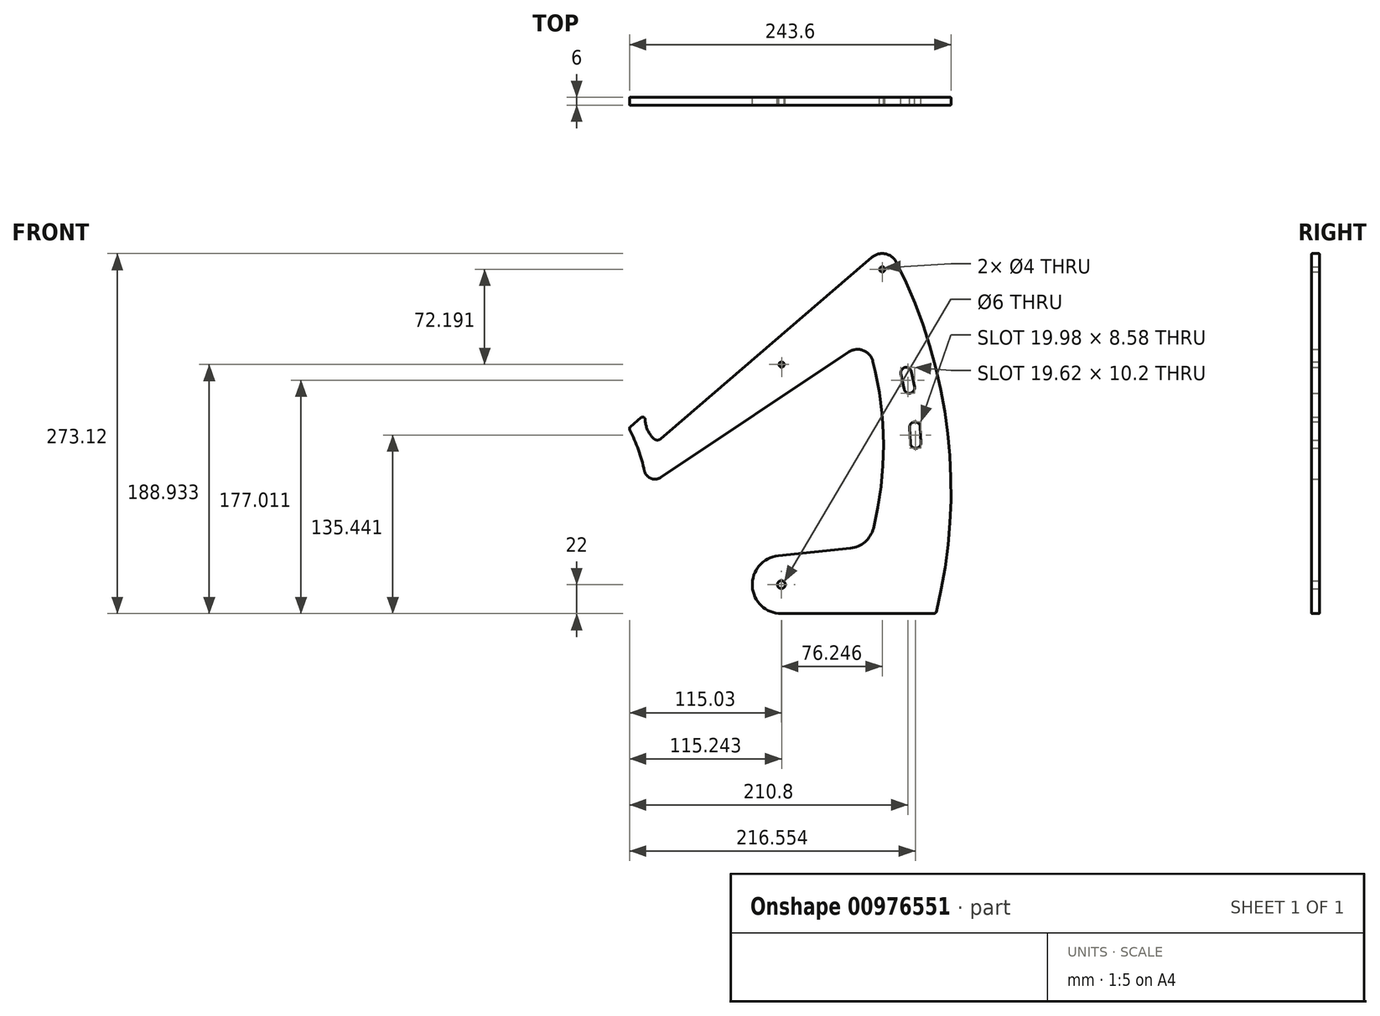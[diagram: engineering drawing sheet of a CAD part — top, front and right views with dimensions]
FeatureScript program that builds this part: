
annotation { "Feature Type Name" : "Feature", "Feature Type Description" : "" }
export const myFeature = defineFeature(function(context is Context, id is Id, definition is map)
    precondition{}
    {
        {
            var Q0;
            Q0=qCreatedBy(makeId("Front.planeOp"),FACE);
            var sketch = newSketch(context, id + "F0", { "sketchPlane" : qUnion([Q0])});
            skLineSegment(sketch, "E0", {"start": v(105, 0) * mm, "end": v(222, 0) * mm});
            skArc(sketch, "E1", {"start": v(3.38, 96.54) * mm, "mid": v(-1.65, 119.28) * mm, "end": v(-10.52, 140.81) * mm});
            skArc(sketch, "E2", {"start": v(222, 0) * mm, "mid": v(230.27, 143.54) * mm, "end": v(185, 280) * mm});
            skLineSegment(sketch, "E3", {"start": v(185, 280) * mm, "end": v(10.64, 130) * mm});
            skLineSegment(sketch, "E4", {"start": v(185, 280) * mm, "end": v(222, 0) * mm, "construction": true});
            skLineSegment(sketch, "E5", {"start": v(10.64, 130) * mm, "end": v(2.37, 151.9) * mm, "construction": true});
            skLineSegment(sketch, "E6", {"start": v(2.37, 151.9) * mm, "end": v(-10.52, 140.81) * mm});
            skArc(sketch, "E7", {"start": v(102.7, 43.88) * mm, "mid": v(83.03, 20.85) * mm, "end": v(105, 0) * mm});
            skLineSegment(sketch, "E8", {"start": v(3.38, 96.54) * mm, "end": v(169.76, 207.53) * mm});
            skLineSegment(sketch, "E9", {"start": v(102.7, 43.88) * mm, "end": v(171, 51.06) * mm});
            skArc(sketch, "E10", {"start": v(171, 51.06) * mm, "mid": v(182.38, 129.39) * mm, "end": v(169.76, 207.53) * mm});
            skLineSegment(sketch, "E11", {"start": v(169.76, 207.53) * mm, "end": v(171, 51.06) * mm, "construction": true});
            skArc(sketch, "E12", {"start": v(2.37, 151.9) * mm, "mid": v(2.5, 142.7) * mm, "end": v(6.73, 134.55) * mm});
            skLineSegment(sketch, "E13", {"start": v(-3.7, 146.68) * mm, "end": v(10.64, 130) * mm, "construction": true});
            skLineSegment(sketch, "E14", {"start": v(6.73, 134.55) * mm, "end": v(10.64, 130) * mm});
            skSolve(sketch);
        }
        {
            var Q0;
            Q0=makeQuery(id+"F0.imprint","IMPRINT",FACE,{"disambiguationData":[TD([[makeQuery(id+"F0.imprint","IMPRINT",EDGE,{"derivedFrom":sQuery(id+"F0.wireOp",EDGE,"E0")}),1.0]])]});
            extrude(context, id + "F1", {"entities" : qUnion([Q0]), "depth" : 6 * mm, "offsetDistance" : 25 * mm});
        }
        {
            var Q0;
            Q0=qCreatedBy(makeId("Front.planeOp"),FACE);
            var sketch = newSketch(context, id + "F2", { "sketchPlane" : qUnion([Q0])});
            skLineSegment(sketch, "E15", {"start": v(199.6, 182.9) * mm, "end": v(177.33, 178.45) * mm, "construction": true});
            skLineSegment(sketch, "E16", {"start": v(199.6, 182.9) * mm, "end": v(221.86, 187.34) * mm, "construction": true});
            skLineSegment(sketch, "E17", {"start": v(195.67, 182.11) * mm, "end": v(198.02, 170.34) * mm});
            skLineSegment(sketch, "E18", {"start": v(203.52, 183.68) * mm, "end": v(205.87, 171.91) * mm});
            skArc(sketch, "E19", {"start": v(203.52, 183.68) * mm, "mid": v(198.81, 186.82) * mm, "end": v(195.67, 182.11) * mm});
            skArc(sketch, "E20", {"start": v(198.02, 170.34) * mm, "mid": v(202.73, 167.2) * mm, "end": v(205.87, 171.91) * mm});
            skLineSegment(sketch, "E21", {"start": v(206.23, 141.43) * mm, "end": v(182.07, 140.24) * mm, "construction": true});
            skLineSegment(sketch, "E22", {"start": v(206.23, 141.43) * mm, "end": v(230.39, 142.63) * mm, "construction": true});
            skLineSegment(sketch, "E23", {"start": v(202.23, 141.24) * mm, "end": v(202.83, 129.25) * mm});
            skLineSegment(sketch, "E24", {"start": v(210.22, 141.63) * mm, "end": v(210.82, 129.65) * mm});
            skArc(sketch, "E25", {"start": v(210.22, 141.63) * mm, "mid": v(206.03, 145.43) * mm, "end": v(202.23, 141.24) * mm});
            skArc(sketch, "E26", {"start": v(202.83, 129.25) * mm, "mid": v(207.02, 125.45) * mm, "end": v(210.82, 129.65) * mm});
            skSolve(sketch);
        }
        {
            var Q0;
            Q0 = qSketchRegion(id + "F2", true);
            extrude(context, id + "F3", {"entities" : qUnion([Q0]), "operationType" : NewBodyOperationType.REMOVE, "endBound" : BoundingType.THROUGH_ALL, "depth" : 25 * mm, "offsetDistance" : 25 * mm});
        }
        {
            var Q0;
            Q0=makeQuery(id+"F1.opExtrude","SWEPT_EDGE",EDGE,{"disambiguationData":[OSD([sQuery(id+"F0.wireOp",EDGE,"E2"),sQuery(id+"F0.wireOp",EDGE,"E3")])]});
            fillet(context, id + "F4", {"entities" : qUnion([Q0]), "radius" : 12 * mm, "tangentPropagation" : true, "defaultsChanged" : true, "vertexSettings" : [], "allowEdgeOverflow" : false});
        }
        {
            var Q0;
            Q0=makeQuery(id+"F1.opExtrude","SWEPT_EDGE",EDGE,{"disambiguationData":[OSD([sQuery(id+"F0.wireOp",EDGE,"E1"),sQuery(id+"F0.wireOp",EDGE,"E8")])]});
            fillet(context, id + "F5", {"entities" : qUnion([Q0]), "radius" : 8 * mm, "tangentPropagation" : true, "allowEdgeOverflow" : false});
        }
        {
            var Q0;
            Q0=makeQuery(id+"F1.opExtrude","SWEPT_EDGE",EDGE,{"disambiguationData":[OSD([sQuery(id+"F0.wireOp",EDGE,"E3"),sQuery(id+"F0.wireOp",EDGE,"E5")])]});
            fillet(context, id + "F6", {"entities" : qUnion([Q0]), "radius" : 4 * mm, "tangentPropagation" : true, "defaultsChanged" : true, "vertexSettings" : [], "allowEdgeOverflow" : false});
        }
        {
            var Q0;
            Q0=makeQuery(id+"F1.opExtrude","SWEPT_EDGE",EDGE,{"disambiguationData":[OSD([sQuery(id+"F0.wireOp",EDGE,"E9"),sQuery(id+"F0.wireOp",EDGE,"E10")])]});
            fillet(context, id + "F7", {"entities" : qUnion([Q0]), "radius" : 20 * mm, "tangentPropagation" : true, "defaultsChanged" : false, "vertexSettings" : [], "allowEdgeOverflow" : false});
        }
        {
            var Q0;
            Q0=makeQuery(id+"F1.opExtrude","SWEPT_EDGE",EDGE,{"disambiguationData":[OSD([sQuery(id+"F0.wireOp",EDGE,"E8"),sQuery(id+"F0.wireOp",EDGE,"E10")])]});
            fillet(context, id + "F8", {"entities" : qUnion([Q0]), "tangentPropagation" : true, "radius" : 12 * mm, "defaultsChanged" : true, "vertexSettings" : [], "allowEdgeOverflow" : false});
        }
        {
            var Q0;
            Q0=qCreatedBy(makeId("Front.planeOp"),FACE);
            var sketch = newSketch(context, id + "F9", { "sketchPlane" : qUnion([Q0])});
            skPoint(sketch, "E27", {"position": v(105, 22) * mm});
            skSolve(sketch);
        }
        {
            var Q0;
            Q0=sQuery(id+"F9.wireOp",VERTEX,"E27");
            var Q1;
            Q1=makeQuery(id+"F1.opExtrude","SWEPT_BODY",BODY,{"disambiguationData":[OSD([sQuery(id+"F0.wireOp",EDGE,"E0"),sQuery(id+"F0.wireOp",EDGE,"E1"),sQuery(id+"F0.wireOp",EDGE,"E2"),sQuery(id+"F0.wireOp",EDGE,"E3"),sQuery(id+"F0.wireOp",EDGE,"E5"),sQuery(id+"F0.wireOp",EDGE,"E6")])]});
            hole(context, id + "F10", {"style" : HoleStyle.SIMPLE, "endStyle" : HoleEndStyle.THROUGH, "oppositeDirection" : true, "holeDiameter" : 6 * mm, "majorDiameter" : 5 * mm, "isTappedThrough" : true, "tappedDepth" : 12 * mm, "tapClearance" : 3, "locations" : qUnion([Q0]), "scope" : qUnion([Q1])});
        }
        {
            var Q0;
            Q0=qCreatedBy(makeId("Front.planeOp"),FACE);
            var sketch = newSketch(context, id + "F11", { "sketchPlane" : qUnion([Q0])});
            skPoint(sketch, "E28", {"position": v(181.46, 261.12) * mm});
            skPoint(sketch, "E29", {"position": v(105.21, 188.93) * mm});
            skLineSegment(sketch, "E30", {"start": v(181.46, 261.12) * mm, "end": v(105.21, 188.93) * mm, "construction": true});
            skSolve(sketch);
        }
        {
            var Q0;
            Q0=sQuery(id+"F11.wireOp",VERTEX,"E29");
            var Q1;
            Q1=sQuery(id+"F11.wireOp",VERTEX,"E28");
            var Q2;
            Q2=makeQuery(id+"F1.opExtrude","SWEPT_BODY",BODY,{"disambiguationData":[OSD([sQuery(id+"F0.wireOp",EDGE,"E0"),sQuery(id+"F0.wireOp",EDGE,"E1"),sQuery(id+"F0.wireOp",EDGE,"E2"),sQuery(id+"F0.wireOp",EDGE,"E3"),sQuery(id+"F0.wireOp",EDGE,"E5"),sQuery(id+"F0.wireOp",EDGE,"E6"),sQuery(id+"F0.wireOp",EDGE,"E7"),sQuery(id+"F0.wireOp",EDGE,"E8"),sQuery(id+"F0.wireOp",EDGE,"E9"),sQuery(id+"F0.wireOp",EDGE,"E10")])]});
            hole(context, id + "F12", {"style" : HoleStyle.SIMPLE, "endStyle" : HoleEndStyle.THROUGH, "oppositeDirection" : true, "holeDiameter" : 4 * mm, "majorDiameter" : 5 * mm, "isTappedThrough" : true, "tappedDepth" : 12 * mm, "tapClearance" : 3, "locations" : qUnion([Q0, Q1]), "scope" : qUnion([Q2])});
        }
        {
            var Q0;
            Q0=makeQuery(id+"F1.opExtrude","SWEPT_EDGE",EDGE,{"disambiguationData":[OSD([sQuery(id+"F0.wireOp",EDGE,"E1"),sQuery(id+"F0.wireOp",EDGE,"E6")])]});
            var Q1;
            Q1=makeQuery(id+"F1.opExtrude","SWEPT_EDGE",EDGE,{"disambiguationData":[OSD([sQuery(id+"F0.wireOp",EDGE,"E5"),sQuery(id+"F0.wireOp",EDGE,"E6")])]});
            var Q2;
            Q2=makeQuery(id+"F1.opExtrude","SWEPT_EDGE",EDGE,{"disambiguationData":[OSD([sQuery(id+"F0.wireOp",EDGE,"E0"),sQuery(id+"F0.wireOp",EDGE,"E2")])]});
            fillet(context, id + "F13", {"entities" : qUnion([Q0, Q1, Q2]), "radius" : 2 * mm, "tangentPropagation" : true, "allowEdgeOverflow" : false});
        }
        {
            var Q0;
            Q0=makeQuery(id+"F1.opExtrude","CAP_EDGE",EDGE,{"disambiguationData":[OSD([sQuery(id+"F0.wireOp",EDGE,"E3")])],"isStart":false});
            var Q1;
            Q1=makeQuery(id+"F1.opExtrude","CAP_EDGE",EDGE,{"disambiguationData":[OSD([sQuery(id+"F0.wireOp",EDGE,"E9")])],"isStart":true});
            var Q2;
            Q2=makeQuery(id+"F1.opExtrude","CAP_EDGE",EDGE,{"disambiguationData":[OSD([sQuery(id+"F0.wireOp",EDGE,"E1")])],"isStart":false});
            var Q3;
            Q3=makeQuery(id+"F1.opExtrude","CAP_EDGE",EDGE,{"disambiguationData":[OSD([sQuery(id+"F0.wireOp",EDGE,"E8")])],"isStart":false});
            var Q4;
            Q4=makeQuery(id+"F1.opExtrude","CAP_EDGE",EDGE,{"disambiguationData":[OSD([sQuery(id+"F0.wireOp",EDGE,"E8")])],"isStart":true});
            var Q5;
            Q5=makeQuery(id+"F3.boolean.opBoolean","INTERSECT",EDGE,{"derivedFrom":[makeQuery(id+"F1.opExtrude","CAP_FACE",FACE,{"disambiguationData":[OSD([sQuery(id+"F0.wireOp",EDGE,"E0"),sQuery(id+"F0.wireOp",EDGE,"E1"),sQuery(id+"F0.wireOp",EDGE,"E2"),sQuery(id+"F0.wireOp",EDGE,"E3"),sQuery(id+"F0.wireOp",EDGE,"E6"),sQuery(id+"F0.wireOp",EDGE,"E7"),sQuery(id+"F0.wireOp",EDGE,"E8"),sQuery(id+"F0.wireOp",EDGE,"E9"),sQuery(id+"F0.wireOp",EDGE,"E10"),sQuery(id+"F0.wireOp",EDGE,"E12")])],"isStart":false}),makeQuery(id+"F3.opExtrude","SWEPT_FACE",FACE,{"disambiguationData":[OSD([sQuery(id+"F2.wireOp",EDGE,"mkxUaUNc-PA2S-2CHY-26pi-s4jNFdiXbWQS")])]})]});
            var Q6;
            Q6=makeQuery(id+"F3.boolean.opBoolean","INTERSECT",EDGE,{"derivedFrom":[makeQuery(id+"F1.opExtrude","CAP_FACE",FACE,{"disambiguationData":[OSD([sQuery(id+"F0.wireOp",EDGE,"E0"),sQuery(id+"F0.wireOp",EDGE,"E1"),sQuery(id+"F0.wireOp",EDGE,"E2"),sQuery(id+"F0.wireOp",EDGE,"E3"),sQuery(id+"F0.wireOp",EDGE,"E6"),sQuery(id+"F0.wireOp",EDGE,"E7"),sQuery(id+"F0.wireOp",EDGE,"E8"),sQuery(id+"F0.wireOp",EDGE,"E9"),sQuery(id+"F0.wireOp",EDGE,"E10"),sQuery(id+"F0.wireOp",EDGE,"E12")])],"isStart":false}),makeQuery(id+"F3.opExtrude","SWEPT_FACE",FACE,{"disambiguationData":[OSD([sQuery(id+"F2.wireOp",EDGE,"SI7QnLGq-xGFz-KG86-VryF-FtgxIGr9pylY")])]})]});
            var Q7;
            Q7=makeQuery(id+"F3.boolean.opBoolean","COPY",EDGE,{"derivedFrom":makeQuery(id+"F3.opExtrude","CAP_EDGE",EDGE,{"disambiguationData":[OSD([sQuery(id+"F2.wireOp",EDGE,"mkxUaUNc-PA2S-2CHY-26pi-s4jNFdiXbWQS")])],"isStart":true})});
            var Q8;
            Q8=makeQuery(id+"F3.boolean.opBoolean","COPY",EDGE,{"derivedFrom":makeQuery(id+"F3.opExtrude","CAP_EDGE",EDGE,{"disambiguationData":[OSD([sQuery(id+"F2.wireOp",EDGE,"SI7QnLGq-xGFz-KG86-VryF-FtgxIGr9pylY")])],"isStart":true})});
            fillet(context, id + "F14", {"entities" : qUnion([Q0, Q1, Q2, Q3, Q4, Q5, Q6, Q7, Q8]), "radius" : 0.5 * mm, "tangentPropagation" : true, "defaultsChanged" : true, "vertexSettings" : [], "allowEdgeOverflow" : false});
        }
    });
